# Revit family: Projector-Canon-REALiS_WUX450ST-D-WUX500(ST)-D_Pro_AV
name_source: partatom
category: Communication Devices
revit_build: Autodesk Revit 2015 (Build: 20160512_1515(x64)
units: mm (PartAtom-declared; Revit-internal decimal feet)

## types (6) — shared parameters
Analog PC Input = WUXGA / UXGA / WSXGA+ / SXGA+ / WXGA+/ FWXGA / WXGA / SXGA / XGA / SVGA / VGA
Apparent Load = 0 VA
Assembly Code = D5030900
C Projector H = 73' - 3 69/256"
Component Video Input = 1080p / 1080i / 720p / 576p / 576i / 480p / 480i
Contrast = 2000:1
Default Elevation = 4' - 0"
Digital PC Input = WUXGA / UXGA / WSXGA+ / SXGA+ / WXGA+/ FWXGA / WXGA / SXGA / XGA / SVGA / VGA
Digital Video Input = 1080p / 1080i / 720p / 576p / 480p
Keynote = Division 27
Lens Shift (Horizontal) = ±10%
Manufacturer = Canon USA Inc.
Model Disclaimer = This 3D model is a simulation of a highly customizable piece of Canon equipment. For assistance in selecting the right Canon equipment for your project, please contact Canon U.S.A., Inc.
Mounting = Upward, Downward, Table, Ceiling
Native Resolution = 1920 x 1200 (WUXGA)
Number of Poles = 1
Power Factor = 1
Power Voltage = AC100 - 240V : 50/60Hz
Product data url = https://bimobject.com
Projection Distances = -
Screen Sizes = -
URL = http://projectors.usa.canon.com
Version = 2014 – v1.0a
Voltage = 100 V

## per-type parameters (varying)
| type | Brightness | C Lens | C Lens Shift | C Projector Shift | Depth | Description | F-Number | Fan Noise | Focal Length | Height | Lens Shift | Lens Shift (Vertical) | Model | Operating Temperature | Power Consumption | Product Documentation Link | Product Page URL | Scanning Frequency | Standby Power | Throw Ratio | Tilt Angle | Type Comments | Weight | Width |
| REALiS WUX450ST Pro AV | 4500lm / 3460lm | 1 | Yes | 0' - 2 15/32" | 1' - 4 21/64" | The REALiS WUX450ST Pro AV Short Throw LCOS Projector combines native WUXGA resolution (1920 x 1200), 4500 lumens of brightness, and Canon's LCOS technology with AISYS-enhancement to project bright, highly-detailed/contrasted and color accurate images - all in a compact size (only 13.9 lbs.). The REALiS WUX450ST's 1.35x optical zoom, short throw ratio of 0.56:1 and 0-75% vertical lens shift help provide exceptional installation flexibility, as does the models HDBaseT™ receiver which allows uncompressed HD video, audio and control signals to be transmitted over one single LAN cable up to a maximum distance of 328ft (100m). | F2.7 | 37 / 30 dB | 8.8mm | 0' - 5 45/128" | V: 0 - 75%, H: ±10% | 0% - 75% | WUX450ST | 32°F - 104°F (0°C - 40°C), 20%RH - 85%RH | 365 / 295W | https://downloads.canon.com | https://www.usa.canon.com | H: 15.734kHz - 75.000kHz, V: 24.000Hz - 60.317Hz | 1.8 - 0.2W | 0.56:1 | - |  | 13.88 lb | 1' - 1 67/256" |
| REALiS WUX450ST D Pro AV | 4500lm / 3460lm | 2 | Yes | 0' - 2 15/32" | 1' - 4 21/64" | The REALiS WUX450ST Pro AV Short Throw LCOS Projector combines native WUXGA resolution (1920 x 1200), 4500 lumens of brightness, and Canon's LCOS technology with AISYS-enhancement to project bright, highly-detailed/contrasted and color accurate images - all in a compact size (only 13.9 lbs.). The REALiS WUX450ST's 1.35x optical zoom, short throw ratio of 0.56:1 and 0-75% vertical lens shift help provide exceptional installation flexibility, as does the models HDBaseT™ receiver which allows uncompressed HD video, audio and control signals to be transmitted over one single LAN cable up to a maximum distance of 328ft (100m). | F2.7 | 37 / 30 dB | 8.8mm | 0' - 5 45/128" | V: 0 - 75%, H: ±10% | 0% - 75% | WUX450ST D | 32°F - 104°F (0°C - 40°C), 20%RH - 85%RH | 365 / 295W | https://www.usa.canon.com | https://www.usa.canon.com | H: 15.734kHz - 75.000kHz, V: 24.000Hz - 60.317Hz | 1.8 - 0.2W | 0.56:1 | - | The WUX450ST D offers a DICOM Simulation Mode (Blue Base and Clear Base color temperature settings) that can reproduce medical images such as X-rays, CAT scans and MRIs for non-diagnostic purposes. | 13.88 lb | 1' - 1 67/256" |
| REALiS WUX500 Pro AV | 5000 Lumens (Normal) / 3800 Lumens (Power Saver) | 3 | No | 0' - 0" | 1' - 2 1/2" | The REALiS WUX500 Pro AV Compact Installation LCOS Projector delivers high performance WUXGA (1920 x 1200) resolution with 5000 lumens of brightness and up to a 2000:1 contrast ratio. These features combined with an advanced Genuine Canon projection lens and Canon's proprietary LCOS technology with AISYS-enhancement helps to produce crisp, bright images with exceptional color reproduction. | F2.8 | 37dB (Full Power) / 30dB (Power Saver) | 21.7 – 39.0mm | 0' - 5 77/256" | Manual V: 0% -60%, H: ±10% | 0% - 60% | WUX500 | 32°F - 104°F (0°C - 40°C) | 365 / 295W | http://downloads.canon.com | https://www.usa.canon.com | - | 1.6 (HDBaseT)0.6 (Network) /0.2 W (Standard) | 1.39 - 2.51:1 | Bottom Front Feet: 2 places (Max. angles: 6° elevation) |  | 13.00 lb | 1' - 1 51/256" |
| REALiS WUX500 D Pro AV | 5000 Lumens (Normal) / 3800 Lumens (Power Saver) | 4 | No | 0' - 0" | 1' - 2 1/2" | The REALiS WUX500 Pro AV Compact Installation LCOS Projector delivers high performance WUXGA (1920 x 1200) resolution with 5000 lumens of brightness and up to a 2000:1 contrast ratio. These features combined with an advanced Genuine Canon projection lens and Canon's proprietary LCOS technology with AISYS-enhancement helps to produce crisp, bright images with exceptional color reproduction. | F2.8 | 37dB (Full Power) / 30dB (Power Saver) | 21.7 – 39.0mm | 0' - 5 77/256" | Manual V: 0% -60%, H: ±10% | 0% - 60% | WUX500 D | 32°F - 104°F (0°C - 40°C) | 365 / 295W | http://downloads.canon.com | https://www.usa.canon.com | - | 1.6 (HDBaseT)0.6 (Network) /0.2 W (Standard) | 1.39 - 2.51:1 | Bottom Front Feet: 2 places (Max. angles: 6° elevation) | The WUX500 D offers a DICOM Simulation Mode (Blue Base and Clear Base color temperature settings) that can reproduce medical images such as X-rays, CAT scans and MRIs for non-diagnostic purposes. | 13.00 lb | 1' - 1 51/256" |
| REALiS WUX500ST Pro AV | 5000lm / 3460lm | 5 | Yes | 0' - 2 15/32" | 1' - 4 21/64" | The REALiS WUX500ST Pro AV Short Throw LCOS Projector combines native WUXGA resolution (1920 x 1200), 4500 lumens of brightness, and Canon's LCOS technology with AISYS-enhancement to project bright, highly-detailed/contrasted and color accurate images - all in a compact size (only 13.9 lbs.). The REALiS WUX500ST's 1.35x optical zoom, short throw ratio of 0.56:1 and 0-75% vertical lens shift help provide exceptional installation flexibility, as does the models HDBaseT™ receiver which allows uncompressed HD video, audio and control signals to be transmitted over one single LAN cable up to a maximum distance of 328ft (100m). | F2.7 | 38 / 30 dB | 8.8mm | 0' - 5 45/128" | V: 0 - 75%, H: ±10% | 0% - 75% | WUX500ST | 32°F - 104°F (0°C - 40°C), 20%RH - 85%RH | 395 / 295W | https://downloads.canon.com | http://www.projectors.usa.canon.com | H: 15.734kHz - 75.000kHz, V: 24.000Hz - 60.317Hz | 1.8 - 0.2W | 0.56:1 | - |  | 13.88 lb | 1' - 1 67/256" |
| REALiS WUX500ST D Pro AV | 5000lm / 3460lm | 6 | Yes | 0' - 2 15/32" | 1' - 4 21/64" | The REALiS WUX500ST Pro AV Short Throw LCOS Projector combines native WUXGA resolution (1920 x 1200), 4500 lumens of brightness, and Canon's LCOS technology with AISYS-enhancement to project bright, highly-detailed/contrasted and color accurate images - all in a compact size (only 13.9 lbs.). The REALiS WUX500ST's 1.35x optical zoom, short throw ratio of 0.56:1 and 0-75% vertical lens shift help provide exceptional installation flexibility, as does the models HDBaseT™ receiver which allows uncompressed HD video, audio and control signals to be transmitted over one single LAN cable up to a maximum distance of 328ft (100m). | F2.7 | 38 / 30 dB | 8.8mm | 0' - 5 45/128" | V: 0 - 75%, H: ±10% | 0% - 75% | WUX500ST D | 32°F - 104°F (0°C - 40°C), 20%RH - 85%RH | 395 / 295W | https://downloads.canon.com | http://www.projectors.usa.canon.com | H: 15.734kHz - 75.000kHz, V: 24.000Hz - 60.317Hz | 1.8 - 0.2W | 0.56:1 | - | The WUX500ST D offers a DICOM Simulation Mode (Blue Base and Clear Base color temperature settings) that can reproduce medical images such as X-rays, CAT scans and MRIs for non-diagnostic purposes. | 13.88 lb | 1' - 1 67/256" |

note: column(s) folded — value = type name in every type: Product Name

## geometry (parser evidence)
native form markers: Sweep x6
no freeform markers — native parametric forms only
